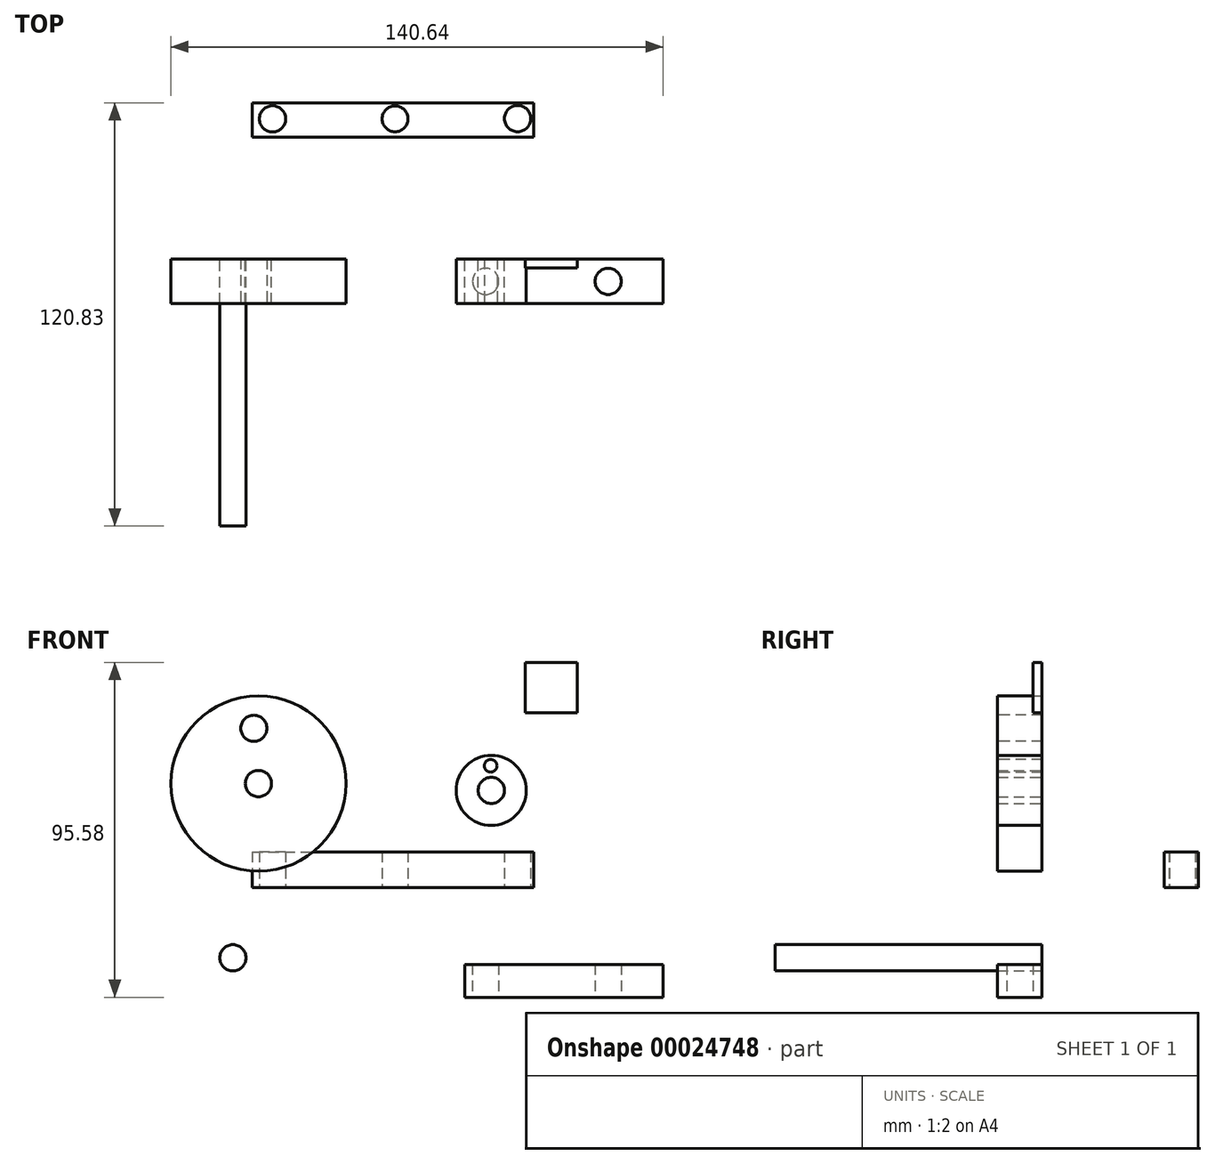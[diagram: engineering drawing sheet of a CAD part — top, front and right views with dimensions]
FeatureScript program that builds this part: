
annotation { "Feature Type Name" : "Feature", "Feature Type Description" : "" }
export const myFeature = defineFeature(function(context is Context, id is Id, definition is map)
    precondition{}
    {
        {
            var Q0;
            Q0=qCreatedBy(makeId("Front.planeOp"),FACE);
            var sketch = newSketch(context, id + "F0", { "sketchPlane" : qUnion([Q0])});
            skCircle(sketch, "E0", {"center": v(-40.11, 29.66) * mm, "radius": 25 * mm});
            skCircle(sketch, "E1", {"center": v(-40.11, 29.66) * mm, "radius": 3.75 * mm});
            skCircle(sketch, "E2", {"center": v(26.4, 27.7) * mm, "radius": 10 * mm});
            skCircle(sketch, "E3", {"center": v(26.4, 27.7) * mm, "radius": 3.75 * mm});
            skSolve(sketch);
        }
        {
            var Q0;
            Q0=qCreatedBy(makeId("Front.planeOp"),FACE);
            var sketch = newSketch(context, id + "F1", { "sketchPlane" : qUnion([Q0])});
            skCircle(sketch, "E4", {"center": v(-47.4, -20.1) * mm, "radius": 3.75 * mm});
            skSolve(sketch);
        }
        {
            var Q0;
            Q0=makeQuery(id+"F1.imprint","IMPRINT",FACE,{"disambiguationData":[TD([[makeQuery(id+"F1.imprint","IMPRINT",EDGE,{"derivedFrom":sQuery(id+"F1.wireOp",EDGE,"E4")}),1.0]])]});
            extrude(context, id + "F2", {"entities" : qUnion([Q0]), "depth" : 76.2 * mm});
        }
        {
            var Q0;
            Q0=makeQuery(id+"F0.imprint","IMPRINT",FACE,{"disambiguationData":[TD([[makeQuery(id+"F0.imprint","IMPRINT",EDGE,{"derivedFrom":sQuery(id+"F0.wireOp",EDGE,"E0")}),1.0]])]});
            var Q1;
            Q1=makeQuery(id+"F0.imprint","IMPRINT",FACE,{"disambiguationData":[TD([[makeQuery(id+"F0.imprint","IMPRINT",EDGE,{"derivedFrom":sQuery(id+"F0.wireOp",EDGE,"E2")}),1.0]])]});
            extrude(context, id + "F3", {"entities" : qUnion([Q0, Q1]), "depth" : 12.7 * mm});
        }
        {
            var Q0;
            Q0=qCreatedBy(makeId("Front.planeOp"),FACE);
            var sketch = newSketch(context, id + "F4", { "sketchPlane" : qUnion([Q0])});
            skLineSegment(sketch, "E5.bottom", {"start": v(18.78, -21.98) * mm, "end": v(75.53, -21.98) * mm});
            skLineSegment(sketch, "E5.top", {"start": v(18.78, -31.36) * mm, "end": v(75.53, -31.36) * mm});
            skLineSegment(sketch, "E5.left", {"start": v(18.78, -21.98) * mm, "end": v(18.78, -31.36) * mm});
            skLineSegment(sketch, "E5.right", {"start": v(75.53, -21.98) * mm, "end": v(75.53, -31.36) * mm});
            skSolve(sketch);
        }
        {
            var Q0;
            Q0=makeQuery(id+"F4.imprint","IMPRINT",FACE,{"disambiguationData":[TD([[makeQuery(id+"F4.imprint","IMPRINT",EDGE,{"derivedFrom":sQuery(id+"F4.wireOp",EDGE,"E5.bottom")}),-1.0]])]});
            extrude(context, id + "F5", {"entities" : qUnion([Q0]), "depth" : 12.7 * mm});
        }
        {
            var Q0;
            Q0=makeQuery(id+"F5.opExtrude","SWEPT_FACE",FACE,{"disambiguationData":[OSD([sQuery(id+"F4.wireOp",EDGE,"E5.top")])]});
            var sketch = newSketch(context, id + "F6", { "sketchPlane" : qUnion([Q0])});
            skCircle(sketch, "E6", {"center": v(24.79, 6.4) * mm, "radius": 3.75 * mm});
            skCircle(sketch, "E7", {"center": v(59.79, 6.4) * mm, "radius": 3.75 * mm});
            skSolve(sketch);
        }
        {
            var Q0;
            Q0=makeQuery(id+"F6.imprint","IMPRINT",FACE,{"disambiguationData":[TD([[makeQuery(id+"F6.imprint","IMPRINT",EDGE,{"derivedFrom":sQuery(id+"F6.wireOp",EDGE,"E6")}),1.0]])]});
            var Q1;
            Q1=makeQuery(id+"F6.imprint","IMPRINT",FACE,{"disambiguationData":[TD([[makeQuery(id+"F6.imprint","IMPRINT",EDGE,{"derivedFrom":sQuery(id+"F6.wireOp",EDGE,"E7")}),1.0]])]});
            extrude(context, id + "F7", {"entities" : qUnion([Q0, Q1]), "operationType" : NewBodyOperationType.REMOVE, "oppositeDirection" : true, "depth" : 25.4 * mm});
        }
        {
            var Q0;
            Q0=qCreatedBy(makeId("Front.planeOp"),FACE);
            var sketch = newSketch(context, id + "F8", { "sketchPlane" : qUnion([Q0])});
            skLineSegment(sketch, "E8.bottom", {"start": v(36.06, 64.22) * mm, "end": v(50.96, 64.22) * mm});
            skLineSegment(sketch, "E8.top", {"start": v(36.06, 49.91) * mm, "end": v(50.96, 49.91) * mm});
            skLineSegment(sketch, "E8.left", {"start": v(36.06, 64.22) * mm, "end": v(36.06, 49.91) * mm});
            skLineSegment(sketch, "E8.right", {"start": v(50.96, 64.22) * mm, "end": v(50.96, 49.91) * mm});
            skSolve(sketch);
        }
        {
            var Q0;
            Q0=makeQuery(id+"F8.imprint","IMPRINT",FACE,{"disambiguationData":[TD([[makeQuery(id+"F8.imprint","IMPRINT",EDGE,{"derivedFrom":sQuery(id+"F8.wireOp",EDGE,"E8.bottom")}),-1.0]])]});
            extrude(context, id + "F9", {"entities" : qUnion([Q0]), "depth" : 2.54 * mm});
        }
        {
            var Q0;
            Q0=makeQuery(id+"F3.opExtrude","CAP_FACE",FACE,{"disambiguationData":[OSD([sQuery(id+"F0.wireOp",EDGE,"E0"),sQuery(id+"F0.wireOp",EDGE,"E1")])],"isStart":false});
            var sketch = newSketch(context, id + "F10", { "sketchPlane" : qUnion([Q0])});
            skCircle(sketch, "E9", {"center": v(-41.42, 45.44) * mm, "radius": 3.73 * mm});
            skSolve(sketch);
        }
        {
            var Q0;
            Q0=makeQuery(id+"F10.imprint","IMPRINT",FACE,{"disambiguationData":[TD([[makeQuery(id+"F10.imprint","IMPRINT",EDGE,{"derivedFrom":sQuery(id+"F10.wireOp",EDGE,"E9")}),1.0]])]});
            extrude(context, id + "F11", {"entities" : qUnion([Q0]), "operationType" : NewBodyOperationType.REMOVE, "oppositeDirection" : true, "depth" : 25.4 * mm});
        }
        {
            var Q0;
            Q0=makeQuery(id+"F3.opExtrude","CAP_FACE",FACE,{"disambiguationData":[OSD([sQuery(id+"F0.wireOp",EDGE,"E2"),sQuery(id+"F0.wireOp",EDGE,"E3")])],"isStart":false});
            var sketch = newSketch(context, id + "F12", { "sketchPlane" : qUnion([Q0])});
            skCircle(sketch, "E10", {"center": v(26.22, 34.72) * mm, "radius": 1.81 * mm});
            skSolve(sketch);
        }
        {
            var Q0;
            Q0=makeQuery(id+"F12.imprint","IMPRINT",FACE,{"disambiguationData":[TD([[makeQuery(id+"F12.imprint","IMPRINT",EDGE,{"derivedFrom":sQuery(id+"F12.wireOp",EDGE,"E10")}),1.0]])]});
            extrude(context, id + "F13", {"entities" : qUnion([Q0]), "operationType" : NewBodyOperationType.REMOVE, "oppositeDirection" : true, "depth" : 25.4 * mm});
        }
        {
            var Q0;
            Q0=qCreatedBy(makeId("Top.planeOp"),FACE);
            var sketch = newSketch(context, id + "F14", { "sketchPlane" : qUnion([Q0])});
            skLineSegment(sketch, "E11.bottom", {"start": v(-41.85, 44.63) * mm, "end": v(38.56, 44.63) * mm});
            skLineSegment(sketch, "E11.top", {"start": v(-41.85, 34.83) * mm, "end": v(38.56, 34.83) * mm});
            skLineSegment(sketch, "E11.left", {"start": v(-41.85, 44.63) * mm, "end": v(-41.85, 34.83) * mm});
            skLineSegment(sketch, "E11.right", {"start": v(38.56, 44.63) * mm, "end": v(38.56, 34.83) * mm});
            skCircle(sketch, "E12", {"center": v(-36.09, 40.02) * mm, "radius": 3.75 * mm});
            skCircle(sketch, "E13", {"center": v(-1.09, 40.02) * mm, "radius": 3.69 * mm});
            skCircle(sketch, "E14", {"center": v(33.91, 40.1) * mm, "radius": 3.75 * mm});
            skSolve(sketch);
        }
        {
            var Q0;
            Q0=makeQuery(id+"F14.imprint","IMPRINT",FACE,{"disambiguationData":[TD([[makeQuery(id+"F14.imprint","IMPRINT",EDGE,{"derivedFrom":sQuery(id+"F14.wireOp",EDGE,"E11.bottom")}),-1.0]])]});
            extrude(context, id + "F15", {"entities" : qUnion([Q0]), "depth" : 10.16 * mm});
        }
    });
